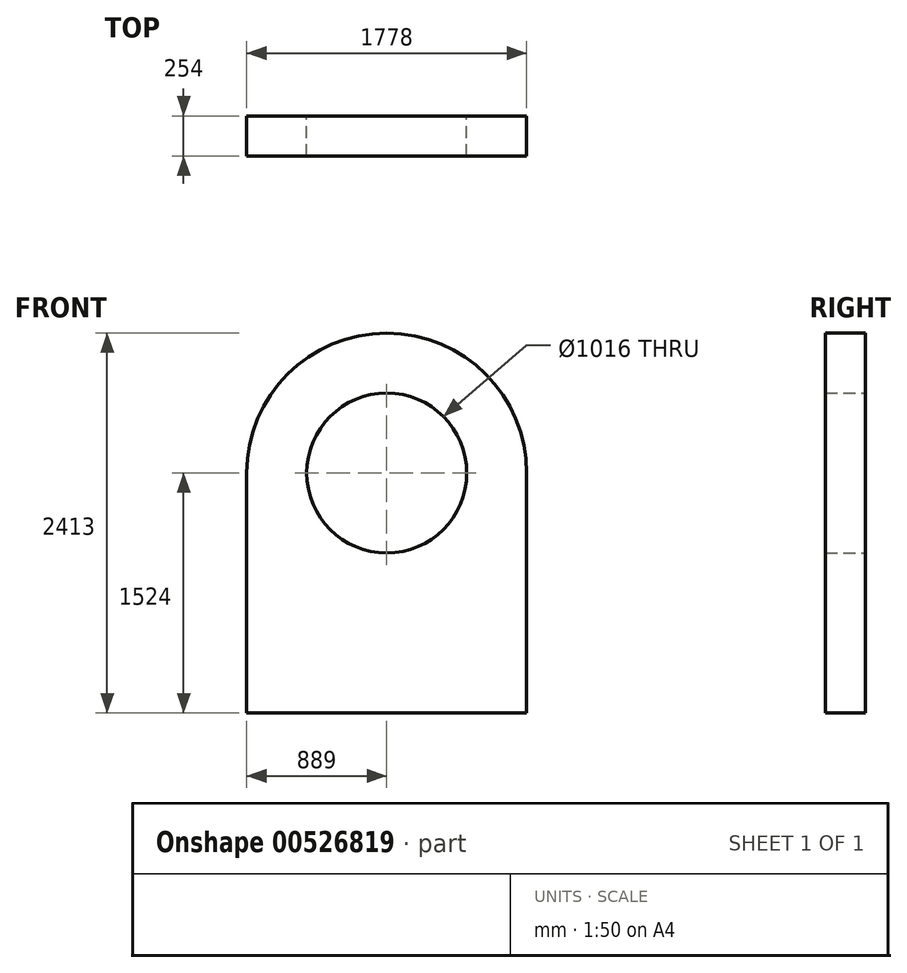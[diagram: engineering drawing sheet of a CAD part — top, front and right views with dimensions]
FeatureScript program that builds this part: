
annotation { "Feature Type Name" : "Feature", "Feature Type Description" : "" }
export const myFeature = defineFeature(function(context is Context, id is Id, definition is map)
    precondition{}
    {
        {
            var Q0;
            Q0=qCreatedBy(makeId("Front.planeOp"),FACE);
            var sketch = newSketch(context, id + "F0", { "sketchPlane" : qUnion([Q0])});
            skLineSegment(sketch, "E0", {"start": v(0, 0) * mm, "end": v(1778, 0) * mm});
            skLineSegment(sketch, "E1", {"start": v(1778, 0) * mm, "end": v(1778, 1524) * mm});
            skLineSegment(sketch, "E2", {"start": v(0, 0) * mm, "end": v(0, 1524) * mm});
            skArc(sketch, "E3", {"start": v(1778, 1524) * mm, "mid": v(889, 2413) * mm, "end": v(0, 1524) * mm});
            skCircle(sketch, "E4", {"center": v(889, 1524) * mm, "radius": 508 * mm});
            skLineSegment(sketch, "E5", {"start": v(254, 456.15) * mm, "end": v(254, 202.15) * mm});
            skLineSegment(sketch, "E6", {"start": v(1524, 456.15) * mm, "end": v(254, 456.15) * mm});
            skLineSegment(sketch, "E7", {"start": v(1524, 456.15) * mm, "end": v(1524, 75.15) * mm});
            skLineSegment(sketch, "E8", {"start": v(1524, 75.15) * mm, "end": v(254, 75.15) * mm});
            skSolve(sketch);
        }
        {
            var Q0;
            Q0=makeQuery(id+"F0.imprint","IMPRINT",FACE,{"disambiguationData":[TD([[makeQuery(id+"F0.imprint","IMPRINT",EDGE,{"derivedFrom":sQuery(id+"F0.wireOp",EDGE,"E0")}),1.0]])]});
            extrude(context, id + "F1", {"entities" : qUnion([Q0]), "depth" : 254 * mm, "offsetDistance" : 25.4 * mm});
        }
    });
